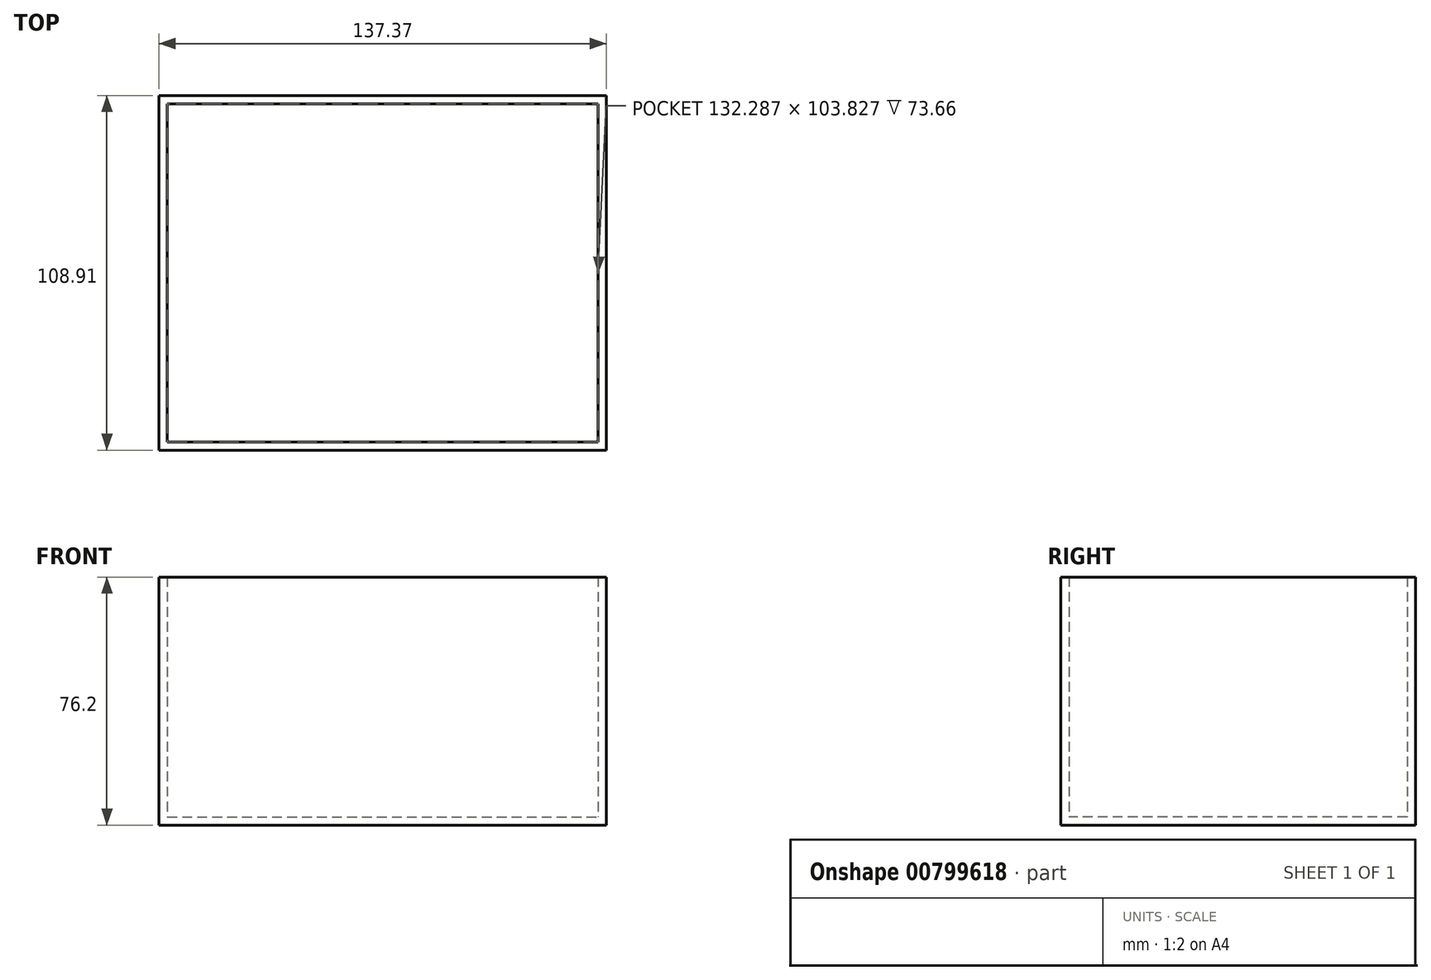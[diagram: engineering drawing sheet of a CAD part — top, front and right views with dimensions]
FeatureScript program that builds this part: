
annotation { "Feature Type Name" : "Feature", "Feature Type Description" : "" }
export const myFeature = defineFeature(function(context is Context, id is Id, definition is map)
    precondition{}
    {
        {
            var Q0;
            Q0=qCreatedBy(makeId("Top.planeOp"),FACE);
            var sketch = newSketch(context, id + "F0", { "sketchPlane" : qUnion([Q0])});
            skLineSegment(sketch, "E0.bottom", {"start": v(-70.72, 52.28) * mm, "end": v(66.65, 52.28) * mm});
            skLineSegment(sketch, "E0.top", {"start": v(-70.72, -56.63) * mm, "end": v(66.65, -56.63) * mm});
            skLineSegment(sketch, "E0.left", {"start": v(-70.72, 52.28) * mm, "end": v(-70.72, -56.63) * mm});
            skLineSegment(sketch, "E0.right", {"start": v(66.65, 52.28) * mm, "end": v(66.65, -56.63) * mm});
            skSolve(sketch);
        }
        {
            var Q0;
            Q0 = qSketchRegion(id + "F0", true);
            var Q1;
            Q1=makeQuery(id+"F0.imprint","IMPRINT",FACE,{"disambiguationData":[TD([[makeQuery(id+"F0.imprint","IMPRINT",EDGE,{"derivedFrom":sQuery(id+"F0.wireOp",EDGE,"E0.bottom")}),-1.0]])]});
            extrude(context, id + "F1", {"entities" : qUnion([Q0, Q1]), "depth" : 76.2 * mm, "offsetDistance" : 25.4 * mm});
        }
        {
            var Q0;
            Q0=makeQuery(id+"F1.opExtrude","CAP_FACE",FACE,{"disambiguationData":[OSD([sQuery(id+"F0.wireOp",EDGE,"E0.bottom"),sQuery(id+"F0.wireOp",EDGE,"E0.top"),sQuery(id+"F0.wireOp",EDGE,"E0.left"),sQuery(id+"F0.wireOp",EDGE,"E0.right")])],"isStart":false});
            shell(context, id + "F2", {"entities" : qUnion([Q0]), "thickness" : 2.54 * mm});
        }
    });
